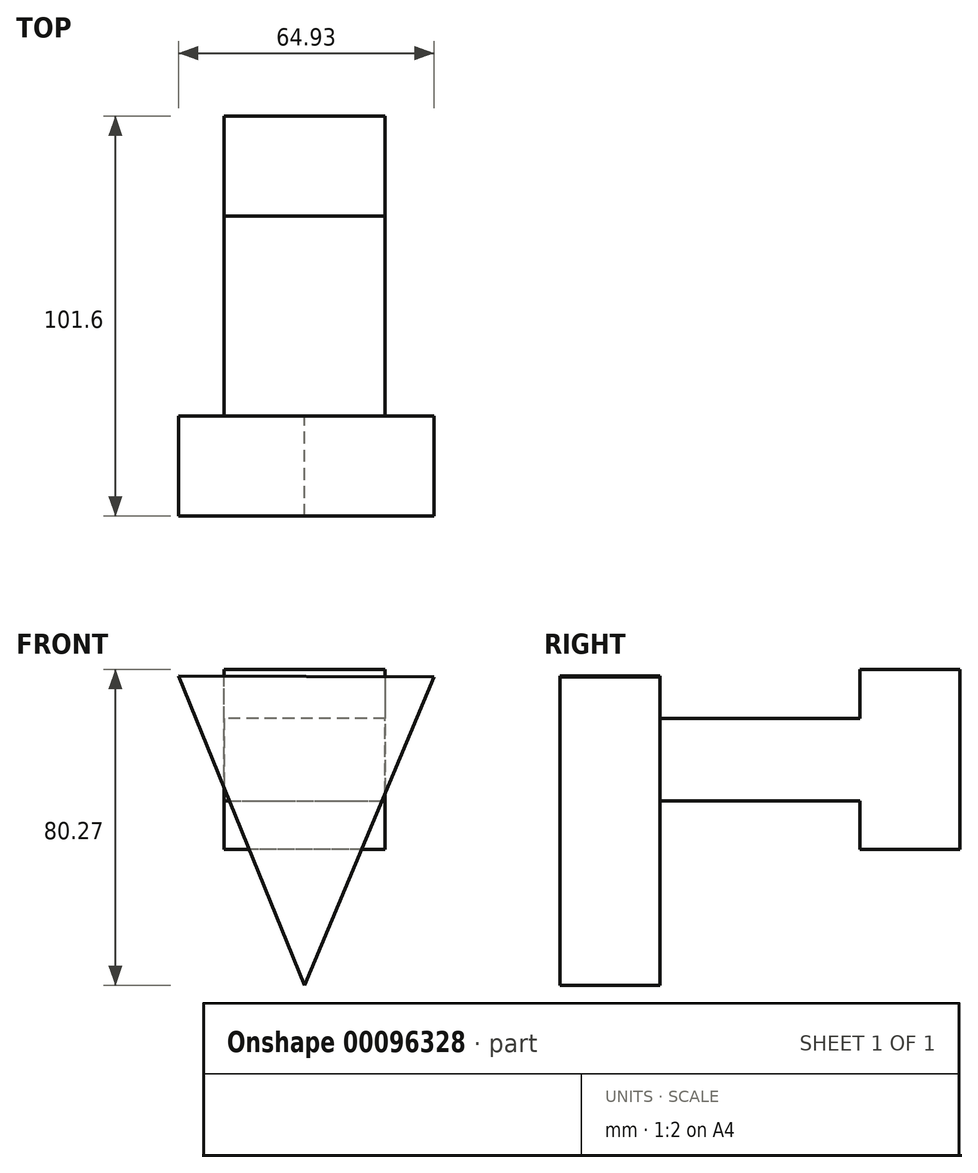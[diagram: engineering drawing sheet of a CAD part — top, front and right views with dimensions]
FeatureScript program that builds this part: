
annotation { "Feature Type Name" : "Feature", "Feature Type Description" : "" }
export const myFeature = defineFeature(function(context is Context, id is Id, definition is map)
    precondition{}
    {
        {
            var Q0;
            Q0=qCreatedBy(makeId("Front.planeOp"),FACE);
            var sketch = newSketch(context, id + "F0", { "sketchPlane" : qUnion([Q0])});
            skLineSegment(sketch, "E0", {"start": v(-69.5, 48.06) * mm, "end": v(-69.5, 27) * mm});
            skLineSegment(sketch, "E1", {"start": v(-69.5, 27) * mm, "end": v(-28.55, 27) * mm});
            skLineSegment(sketch, "E2", {"start": v(-28.55, 27) * mm, "end": v(-28.55, 48.06) * mm});
            skLineSegment(sketch, "E3", {"start": v(-28.55, 48.06) * mm, "end": v(-69.5, 48.06) * mm});
            skSolve(sketch);
        }
        {
            var Q0;
            Q0 = qSketchRegion(id + "F0", true);
            extrude(context, id + "F1", {"entities" : qUnion([Q0]), "depth" : 50.8 * mm});
        }
        {
            var Q0;
            Q0=makeQuery(id+"F1.opExtrude","CAP_FACE",FACE,{"disambiguationData":[OSD([sQuery(id+"F0.wireOp",EDGE,"E0"),sQuery(id+"F0.wireOp",EDGE,"E1"),sQuery(id+"F0.wireOp",EDGE,"E2"),sQuery(id+"F0.wireOp",EDGE,"E3")])],"isStart":false});
            var sketch = newSketch(context, id + "F2", { "sketchPlane" : qUnion([Q0])});
            skLineSegment(sketch, "E4", {"start": v(-81.07, 58.87) * mm, "end": v(-49.02, -19.82) * mm});
            skPoint(sketch, "E4.endSnap0", {"position": v(-49.02, 27) * mm});
            skLineSegment(sketch, "E5", {"start": v(-49.02, -19.82) * mm, "end": v(-16.14, 58.54) * mm});
            skPoint(sketch, "E6.orphan", {"position": v(-19.61, 50.27) * mm});
            skPoint(sketch, "E7.orphan", {"position": v(-77.57, 50.27) * mm});
            skLineSegment(sketch, "E8", {"start": v(-81.07, 58.87) * mm, "end": v(-16.14, 58.54) * mm});
            skSolve(sketch);
        }
        {
            var Q0;
            Q0 = qSketchRegion(id + "F2", true);
            extrude(context, id + "F3", {"entities" : qUnion([Q0]), "operationType" : NewBodyOperationType.ADD, "depth" : 25.4 * mm});
        }
        {
            var Q0;
            Q0=makeQuery(id+"F1.opExtrude","CAP_FACE",FACE,{"disambiguationData":[OSD([sQuery(id+"F0.wireOp",EDGE,"E0"),sQuery(id+"F0.wireOp",EDGE,"E1"),sQuery(id+"F0.wireOp",EDGE,"E2"),sQuery(id+"F0.wireOp",EDGE,"E3")])],"isStart":true});
            var sketch = newSketch(context, id + "F4", { "sketchPlane" : qUnion([Q0])});
            skLineSegment(sketch, "E9", {"start": v(28.55, 60.45) * mm, "end": v(28.55, 14.78) * mm});
            skLineSegment(sketch, "E10", {"start": v(28.55, 14.78) * mm, "end": v(69.5, 14.78) * mm});
            skLineSegment(sketch, "E11", {"start": v(69.5, 14.78) * mm, "end": v(69.5, 60.45) * mm});
            skLineSegment(sketch, "E12", {"start": v(69.5, 60.45) * mm, "end": v(28.55, 60.45) * mm});
            skSolve(sketch);
        }
        {
            var Q0;
            Q0 = qSketchRegion(id + "F4", true);
            extrude(context, id + "F5", {"entities" : qUnion([Q0]), "operationType" : NewBodyOperationType.ADD, "depth" : 25.4 * mm});
        }
    });
